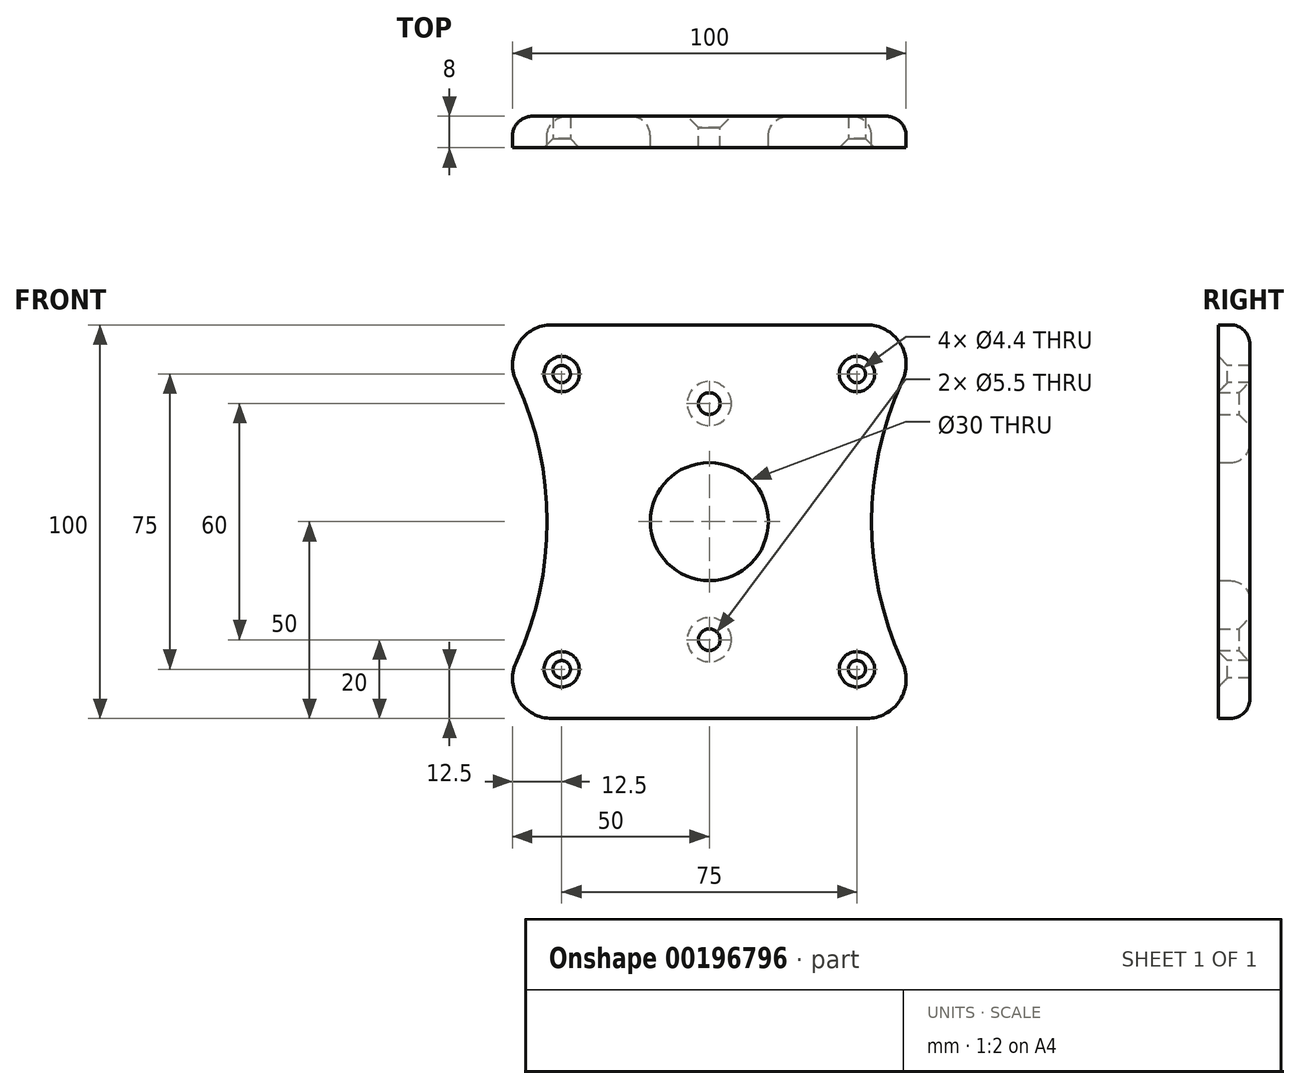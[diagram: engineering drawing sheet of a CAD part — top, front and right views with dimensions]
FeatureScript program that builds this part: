
annotation { "Feature Type Name" : "Feature", "Feature Type Description" : "" }
export const myFeature = defineFeature(function(context is Context, id is Id, definition is map)
    precondition{}
    {
        {
            var Q0;
            Q0=qCreatedBy(makeId("Front.planeOp"),FACE);
            var sketch = newSketch(context, id + "F0", { "sketchPlane" : qUnion([Q0])});
            skArc(sketch, "E0.filletArc", {"start": v(-40, 50) * mm, "mid": v(-48.4, 45.42) * mm, "end": v(-49.1, 35.88) * mm});
            skArc(sketch, "E1", {"start": v(-48.84, -35.27) * mm, "mid": v(-41.22, 0) * mm, "end": v(-48.84, 35.27) * mm});
            skLineSegment(sketch, "E2", {"start": v(-126.74, 0) * mm, "end": v(0, 0) * mm, "construction": true});
            skPoint(sketch, "E3.center", {"position": v(0, 0) * mm});
            skCircle(sketch, "E4", {"center": v(0, 0) * mm, "radius": 15 * mm});
            skLineSegment(sketch, "E5", {"start": v(-48.84, 35.27) * mm, "end": v(-49.1, 35.88) * mm});
            skLineSegment(sketch, "E6.MirrorCS", {"start": v(-48.84, -35.27) * mm, "end": v(-49.1, -35.88) * mm});
            skArc(sketch, "E7.MirrorCS", {"start": v(-40, -50) * mm, "mid": v(-48.4, -45.42) * mm, "end": v(-49.1, -35.88) * mm});
            skArc(sketch, "E8.1.0", {"start": v(40, -50) * mm, "mid": v(48.4, -45.42) * mm, "end": v(49.1, -35.88) * mm});
            skLineSegment(sketch, "E8.1.1", {"start": v(48.84, -35.27) * mm, "end": v(49.1, -35.88) * mm});
            skArc(sketch, "E8.1.2", {"start": v(48.84, 35.27) * mm, "mid": v(41.22, 0) * mm, "end": v(48.84, -35.27) * mm});
            skLineSegment(sketch, "E8.1.3", {"start": v(48.84, 35.27) * mm, "end": v(49.1, 35.88) * mm});
            skArc(sketch, "E8.1.4", {"start": v(40, 50) * mm, "mid": v(48.4, 45.42) * mm, "end": v(49.1, 35.88) * mm});
            skLineSegment(sketch, "E9", {"start": v(-40, 50) * mm, "end": v(40, 50) * mm});
            skLineSegment(sketch, "E10", {"start": v(-40, -50) * mm, "end": v(40, -50) * mm});
            skSolve(sketch);
        }
        {
            var Q0;
            Q0=qSketchRegion(id+"F0",true);
            extrude(context, id + "F1", {"entities" : qUnion([Q0]), "depth" : 8 * mm});
        }
        {
            var Q0;
            Q0=makeQuery(id+"F1.opExtrude","CAP_FACE",FACE,{"disambiguationData":[OSD([sQuery(id+"F0.wireOp",EDGE,"80d8c59e-0251-4716-a2c8-4363b32e0156.bottom"),sQuery(id+"F0.wireOp",EDGE,"80d8c59e-0251-4716-a2c8-4363b32e0156.top"),sQuery(id+"F0.wireOp",EDGE,"80d8c59e-0251-4716-a2c8-4363b32e0156.left"),sQuery(id+"F0.wireOp",EDGE,"80d8c59e-0251-4716-a2c8-4363b32e0156.right"),sQuery(id+"F0.wireOp",EDGE,"E0.filletArc"),sQuery(id+"F0.wireOp",EDGE,"d2e91a69-8f18-4414-8b59-9c0fbf4dc26e.filletArc"),sQuery(id+"F0.wireOp",EDGE,"d28fec5a-6cee-4a2d-8b0c-cb9c8f74a6da.filletArc"),sQuery(id+"F0.wireOp",EDGE,"2173d963-f5cd-4cbe-9097-862afaaeb454.filletArc")])],"isStart":false});
            var sketch = newSketch(context, id + "F2", { "sketchPlane" : qUnion([Q0])});
            skPoint(sketch, "E11", {"position": v(-37.5, 37.5) * mm});
            skPoint(sketch, "E12", {"position": v(-37.5, -37.5) * mm});
            skPoint(sketch, "E13", {"position": v(37.5, 37.5) * mm});
            skPoint(sketch, "E14", {"position": v(37.5, -37.5) * mm});
            skSolve(sketch);
        }
        {
            var Q0;
            Q0=sQuery(id+"F2.wireOp",VERTEX,"0452b4d8-1937-40ba-a99a-d7e28835a7c5");
            var Q1;
            Q1=sQuery(id+"F2.wireOp",VERTEX,"1c9d2db2-a8f9-4dac-88bc-95ce254ce440");
            var Q2;
            Q2=sQuery(id+"F2.wireOp",VERTEX,"33c01a18-1348-4d26-ac3b-41b8eca9d244");
            var Q3;
            Q3=sQuery(id+"F2.wireOp",VERTEX,"0f962127-864a-4965-81ac-c4c549ad2cfd");
            var Q4;
            Q4=sQuery(id+"F2.wireOp",VERTEX,"E11");
            var Q5;
            Q5=sQuery(id+"F2.wireOp",VERTEX,"E13");
            var Q6;
            Q6=sQuery(id+"F2.wireOp",VERTEX,"E14");
            var Q7;
            Q7=sQuery(id+"F2.wireOp",VERTEX,"E12");
            var Q8;
            Q8=makeQuery(id+"F1.opExtrude","SWEPT_BODY",BODY,{"disambiguationData":[OSD([sQuery(id+"F0.wireOp",EDGE,"80d8c59e-0251-4716-a2c8-4363b32e0156.bottom"),sQuery(id+"F0.wireOp",EDGE,"80d8c59e-0251-4716-a2c8-4363b32e0156.top"),sQuery(id+"F0.wireOp",EDGE,"80d8c59e-0251-4716-a2c8-4363b32e0156.left"),sQuery(id+"F0.wireOp",EDGE,"80d8c59e-0251-4716-a2c8-4363b32e0156.right"),sQuery(id+"F0.wireOp",EDGE,"E0.filletArc"),sQuery(id+"F0.wireOp",EDGE,"d2e91a69-8f18-4414-8b59-9c0fbf4dc26e.filletArc"),sQuery(id+"F0.wireOp",EDGE,"d28fec5a-6cee-4a2d-8b0c-cb9c8f74a6da.filletArc"),sQuery(id+"F0.wireOp",EDGE,"2173d963-f5cd-4cbe-9097-862afaaeb454.filletArc")])]});
            hole(context, id + "F3", {"style" : HoleStyle.C_SINK, "endStyle" : HoleEndStyle.THROUGH, "standardTappedOrClearance" : lookupTablePath({ "standard" : "ISO", "fit" : "Normal", "size" : "M4", "type" : "Clearance" }), "standardBlindInLast" : lookupTablePath({ "fit" : "Standard", "standard" : "ISO", "size" : "M4", "type" : "Clearance" }), "holeDiameter" : 4.4 * mm, "cSinkDiameter" : 8.96 * mm, "cSinkAngle" : 90 * degree, "locations" : qUnion([Q0, Q1, Q2, Q3, Q4, Q5, Q6, Q7]), "scope" : qUnion([Q8]), "isTappedThrough" : true});
        }
        {
            var Q0;
            Q0=makeQuery(id+"F1.opExtrude","CAP_FACE",FACE,{"disambiguationData":[OSD([sQuery(id+"F0.wireOp",EDGE,"80d8c59e-0251-4716-a2c8-4363b32e0156.bottom"),sQuery(id+"F0.wireOp",EDGE,"80d8c59e-0251-4716-a2c8-4363b32e0156.top"),sQuery(id+"F0.wireOp",EDGE,"80d8c59e-0251-4716-a2c8-4363b32e0156.left"),sQuery(id+"F0.wireOp",EDGE,"80d8c59e-0251-4716-a2c8-4363b32e0156.right"),sQuery(id+"F0.wireOp",EDGE,"E0.filletArc"),sQuery(id+"F0.wireOp",EDGE,"d2e91a69-8f18-4414-8b59-9c0fbf4dc26e.filletArc"),sQuery(id+"F0.wireOp",EDGE,"d28fec5a-6cee-4a2d-8b0c-cb9c8f74a6da.filletArc"),sQuery(id+"F0.wireOp",EDGE,"2173d963-f5cd-4cbe-9097-862afaaeb454.filletArc")])],"isStart":true});
            var sketch = newSketch(context, id + "F4", { "sketchPlane" : qUnion([Q0])});
            skPoint(sketch, "E15", {"position": v(0, 30) * mm});
            skPoint(sketch, "E16", {"position": v(0, -30) * mm});
            skSolve(sketch);
        }
        {
            var Q0;
            Q0=sQuery(id+"F4.wireOp",VERTEX,"E16");
            var Q1;
            Q1=sQuery(id+"F4.wireOp",VERTEX,"E15");
            var Q2;
            Q2=makeQuery(id+"F1.opExtrude","SWEPT_BODY",BODY,{"disambiguationData":[OSD([sQuery(id+"F0.wireOp",EDGE,"80d8c59e-0251-4716-a2c8-4363b32e0156.bottom"),sQuery(id+"F0.wireOp",EDGE,"80d8c59e-0251-4716-a2c8-4363b32e0156.top"),sQuery(id+"F0.wireOp",EDGE,"80d8c59e-0251-4716-a2c8-4363b32e0156.left"),sQuery(id+"F0.wireOp",EDGE,"80d8c59e-0251-4716-a2c8-4363b32e0156.right"),sQuery(id+"F0.wireOp",EDGE,"E0.filletArc"),sQuery(id+"F0.wireOp",EDGE,"d2e91a69-8f18-4414-8b59-9c0fbf4dc26e.filletArc"),sQuery(id+"F0.wireOp",EDGE,"d28fec5a-6cee-4a2d-8b0c-cb9c8f74a6da.filletArc"),sQuery(id+"F0.wireOp",EDGE,"2173d963-f5cd-4cbe-9097-862afaaeb454.filletArc")])]});
            hole(context, id + "F5", {"style" : HoleStyle.C_SINK, "endStyle" : HoleEndStyle.THROUGH, "standardTappedOrClearance" : lookupTablePath({ "standard" : "ISO", "fit" : "Normal", "size" : "M5", "type" : "Clearance" }), "standardBlindInLast" : lookupTablePath({ "fit" : "Standard", "standard" : "ISO", "size" : "M5", "type" : "Clearance" }), "holeDiameter" : 5.5 * mm, "cSinkDiameter" : 11.2 * mm, "cSinkAngle" : 90 * degree, "locations" : qUnion([Q0, Q1]), "scope" : qUnion([Q2]), "isTappedThrough" : true});
        }
        {
            var Q0;
            Q0=makeQuery(id+"F1.opExtrude","CAP_EDGE",EDGE,{"disambiguationData":[OSD([sQuery(id+"F0.wireOp",EDGE,"E9")])],"isStart":true});
            var Q1;
            Q1=makeQuery(id+"F1.opExtrude","CAP_EDGE",EDGE,{"disambiguationData":[OSD([sQuery(id+"F0.wireOp",EDGE,"E4")])],"isStart":true});
            fillet(context, id + "F6", {"entities" : qUnion([Q0, Q1]), "radius" : 5 * mm, "tangentPropagation" : true, "allowEdgeOverflow" : false});
        }
    });
